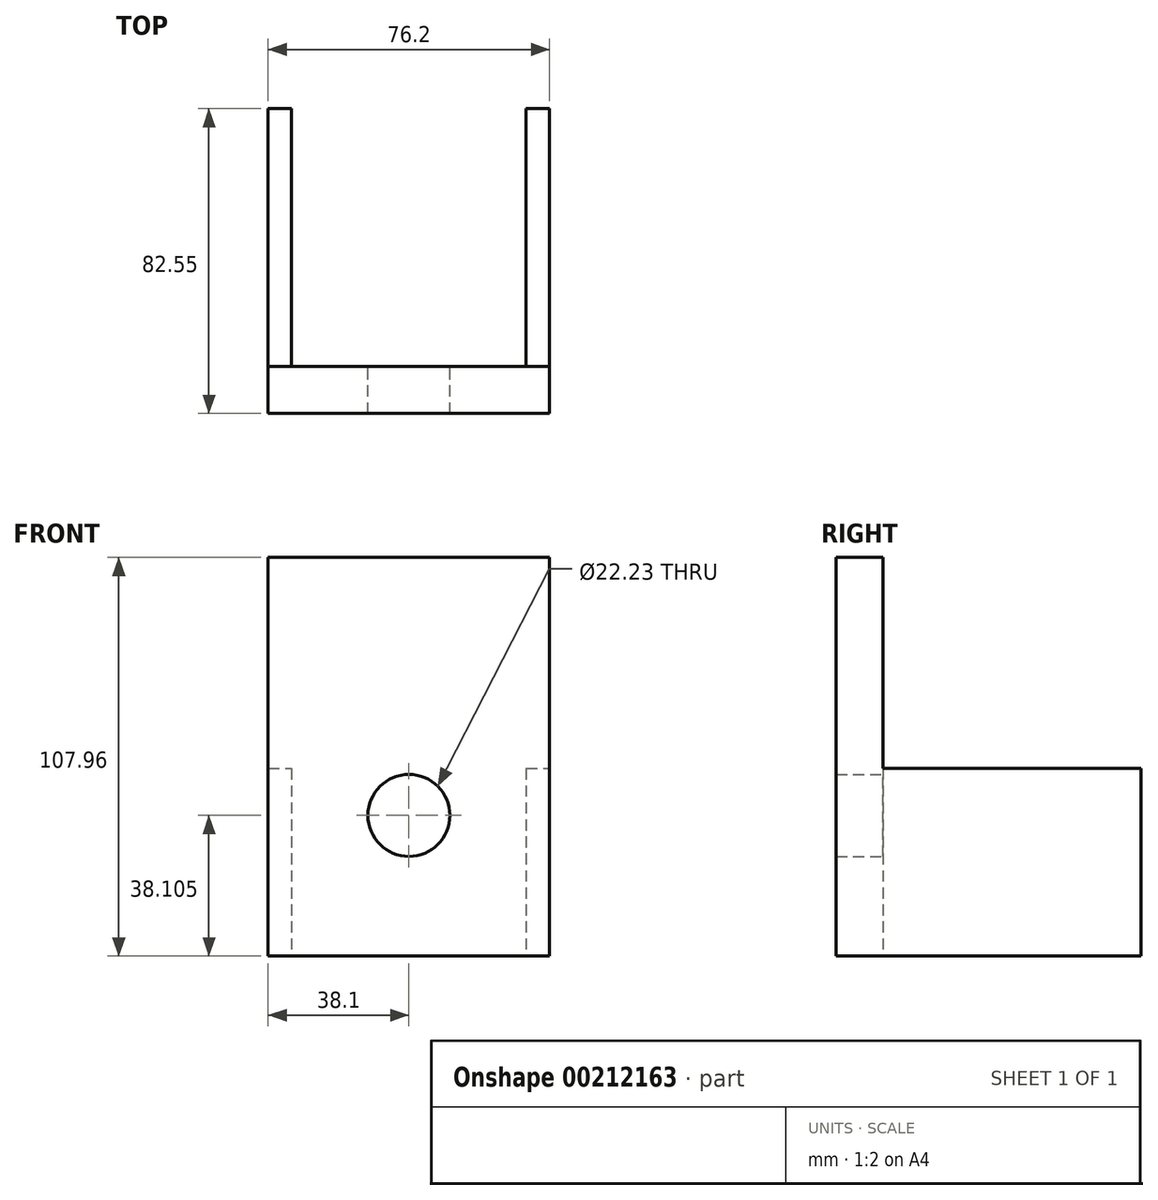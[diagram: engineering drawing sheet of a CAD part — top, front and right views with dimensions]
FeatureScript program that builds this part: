
annotation { "Feature Type Name" : "Feature", "Feature Type Description" : "" }
export const myFeature = defineFeature(function(context is Context, id is Id, definition is map)
    precondition{}
    {
        {
            var Q0;
            Q0=qCreatedBy(makeId("Front.planeOp"),FACE);
            var sketch = newSketch(context, id + "F0", { "sketchPlane" : qUnion([Q0])});
            skLineSegment(sketch, "E0.bottom", {"start": v(-38.1, 53.97) * mm, "end": v(38.1, 53.97) * mm});
            skLineSegment(sketch, "E0.top", {"start": v(-38.1, -53.97) * mm, "end": v(38.1, -53.97) * mm});
            skLineSegment(sketch, "E0.left", {"start": v(-38.1, 53.97) * mm, "end": v(-38.1, -53.98) * mm});
            skLineSegment(sketch, "E0.right", {"start": v(38.1, 53.97) * mm, "end": v(38.1, -53.97) * mm});
            skPoint(sketch, "E0.middle", {"position": v(0, 0) * mm});
            skCircle(sketch, "E1", {"center": v(0, -15.87) * mm, "radius": 11.11 * mm});
            skSolve(sketch);
        }
        {
            var Q0;
            Q0=makeQuery(id+"F0.imprint","IMPRINT",FACE,{"disambiguationData":[TD([[makeQuery(id+"F0.imprint","IMPRINT",EDGE,{"derivedFrom":sQuery(id+"F0.wireOp",EDGE,"E0.bottom")}),-1.0]])]});
            extrude(context, id + "F1", {"entities" : qUnion([Q0]), "depth" : 12.7 * mm});
        }
        {
            var Q0;
            Q0=makeQuery(id+"F1.opExtrude","SWEPT_FACE",FACE,{"disambiguationData":[OSD([sQuery(id+"F0.wireOp",EDGE,"E0.right")])]});
            var sketch = newSketch(context, id + "F2", { "sketchPlane" : qUnion([Q0])});
            skLineSegment(sketch, "E2", {"start": v(0, -53.97) * mm, "end": v(69.85, -53.97) * mm});
            skLineSegment(sketch, "E3", {"start": v(69.85, -53.97) * mm, "end": v(69.85, -3.17) * mm});
            skLineSegment(sketch, "E4", {"start": v(69.85, -3.17) * mm, "end": v(0, -3.17) * mm});
            skSolve(sketch);
        }
        {
            var Q0;
            {var subQ0=sQuery(id+"F2.wireOp",EDGE,"E2");Q0=makeQuery(id+"F2.imprint","IMPRINT",FACE,{"disambiguationData":[TD([[makeQuery(id+"F2.imprint","IMPRINT",EDGE,{"derivedFrom":subQ0}),1.0]])]});}
            extrude(context, id + "F3", {"entities" : qUnion([Q0]), "operationType" : NewBodyOperationType.ADD, "oppositeDirection" : true, "depth" : 6.35 * mm});
        }
        {
            var Q0;
            {var subQ0=sQuery(id+"F2.wireOp",EDGE,"E2");Q0=makeQuery(id+"F2.imprint","IMPRINT",FACE,{"disambiguationData":[TD([[makeQuery(id+"F2.imprint","IMPRINT",EDGE,{"derivedFrom":subQ0}),1.0]])]});}
            extrude(context, id + "F4", {"entities" : qUnion([Q0]), "operationType" : NewBodyOperationType.ADD, "oppositeDirection" : true, "depth" : 76.2 * mm, "hasSecondDirection" : true, "secondDirectionOppositeDirection" : true, "secondDirectionDepth" : 69.85 * mm});
        }
        {
            var Q0;
            Q0=makeQuery(id+"F4.opExtrude","SWEPT_FACE",FACE,{"disambiguationData":[OSD([sQuery(id+"F2.wireOp",EDGE,"E3")])]});
            var sketch = newSketch(context, id + "F5", { "sketchPlane" : qUnion([Q0])});
            skLineSegment(sketch, "E5", {"start": v(0, 0) * mm, "end": v(0, -53.98) * mm, "construction": true});
            skLineSegment(sketch, "E6", {"start": v(0, -15.87) * mm, "end": v(-23.2, -15.87) * mm, "construction": true});
            skSolve(sketch);
        }
    });
